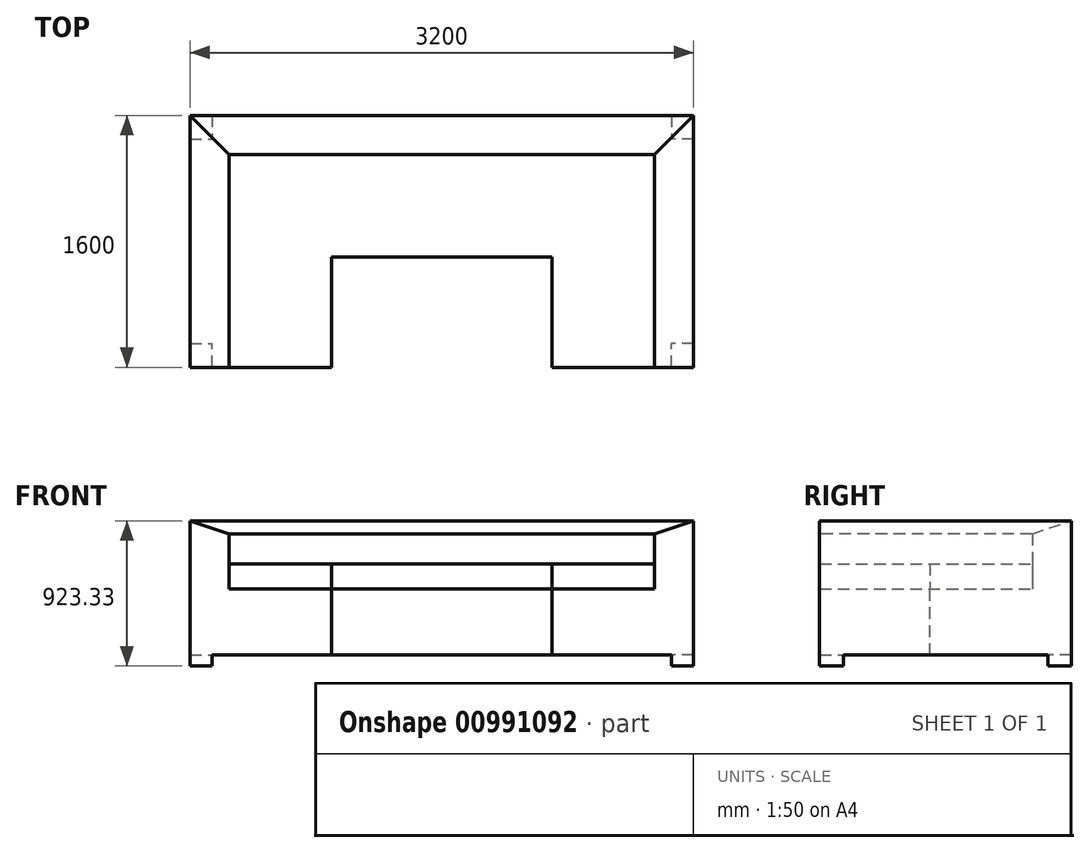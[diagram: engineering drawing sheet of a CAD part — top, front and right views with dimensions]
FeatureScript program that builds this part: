
annotation { "Feature Type Name" : "Feature", "Feature Type Description" : "" }
export const myFeature = defineFeature(function(context is Context, id is Id, definition is map)
    precondition{}
    {
        {
            var Q0;
            Q0=qCreatedBy(makeId("Top.planeOp"),FACE);
            var sketch = newSketch(context, id + "F0", { "sketchPlane" : qUnion([Q0])});
            skLineSegment(sketch, "E0.bottom", {"start": v(0, 0) * mm, "end": v(-900, 0) * mm});
            skLineSegment(sketch, "E0.top", {"start": v(0, 1600) * mm, "end": v(-900, 1600) * mm});
            skLineSegment(sketch, "E0.left", {"start": v(0, 0) * mm, "end": v(0, 1600) * mm});
            skLineSegment(sketch, "E0.right", {"start": v(-900, 0) * mm, "end": v(-900, 700) * mm});
            skLineSegment(sketch, "E1.bottom", {"start": v(-900, 1600) * mm, "end": v(-2300, 1600) * mm});
            skLineSegment(sketch, "E1.top", {"start": v(-900, 700) * mm, "end": v(-2300, 700) * mm});
            skLineSegment(sketch, "E2", {"start": v(-1600, 1600) * mm, "end": v(-1600, 700) * mm, "construction": true});
            skLineSegment(sketch, "E3.MirrorCS", {"start": v(-3200, 1600) * mm, "end": v(-2300, 1600) * mm});
            skLineSegment(sketch, "E4.MirrorCS", {"start": v(-3200, 0) * mm, "end": v(-3200, 1600) * mm});
            skLineSegment(sketch, "E5.MirrorCS", {"start": v(-3200, 0) * mm, "end": v(-2300, 0) * mm});
            skLineSegment(sketch, "E6.MirrorCS", {"start": v(-2300, 0) * mm, "end": v(-2300, 700) * mm});
            skPoint(sketch, "E7.MirrorCS.end.orphan", {"position": v(-2300, 700) * mm});
            skPoint(sketch, "E7.MirrorCS.start.orphan", {"position": v(-2300, 1600) * mm});
            skLineSegment(sketch, "E8.0", {"start": v(-250, 0) * mm, "end": v(-250, 1350) * mm});
            skLineSegment(sketch, "E8.1", {"start": v(-2950, 0) * mm, "end": v(-2950, 1350) * mm});
            skLineSegment(sketch, "E8.2", {"start": v(-2950, 1350) * mm, "end": v(-1600, 1350) * mm});
            skLineSegment(sketch, "E8.3", {"start": v(-900, 1350) * mm, "end": v(-1600, 1350) * mm});
            skLineSegment(sketch, "E8.4", {"start": v(-250, 1350) * mm, "end": v(-900, 1350) * mm});
            skLineSegment(sketch, "E9", {"start": v(-900, 1600) * mm, "end": v(-900, 700) * mm, "construction": true});
            skLineSegment(sketch, "E10", {"start": v(-3200, 1480.04) * mm, "end": v(0, 1480.04) * mm, "construction": true});
            skSolve(sketch);
        }
        {
            var Q0;
            Q0 = qSketchRegion(id + "F0", true);
            extrude(context, id + "F1", {"entities" : qUnion([Q0]), "oppositeDirection" : true, "depth" : 420 * mm, "offsetDistance" : 25 * mm});
        }
        {
            var Q0;
            Q0=makeQuery(id+"F0.imprint","IMPRINT",FACE,{"disambiguationData":[TD([[makeQuery(id+"F0.imprint","IMPRINT",EDGE,{"derivedFrom":sQuery(id+"F0.wireOp",EDGE,"E0.top")}),1.0]])]});
            extrude(context, id + "F2", {"entities" : qUnion([Q0]), "operationType" : NewBodyOperationType.ADD, "depth" : 450 * mm, "offsetDistance" : 25 * mm});
        }
        {
            var Q0;
            Q0=makeQuery(id+"F2.opExtrude","CAP_EDGE",EDGE,{"disambiguationData":[OSD([sQuery(id+"F0.wireOp",EDGE,"E8.0")])],"isStart":false});
            var Q1;
            Q1=makeQuery(id+"F2.opExtrude","CAP_EDGE",EDGE,{"disambiguationData":[OSD([sQuery(id+"F0.wireOp",EDGE,"E8.3"),sQuery(id+"F0.wireOp",EDGE,"E8.4")])],"isStart":false});
            var Q2;
            Q2=makeQuery(id+"F2.opExtrude","CAP_EDGE",EDGE,{"disambiguationData":[OSD([sQuery(id+"F0.wireOp",EDGE,"E8.2")])],"isStart":false});
            var Q3;
            Q3=makeQuery(id+"F2.opExtrude","CAP_EDGE",EDGE,{"disambiguationData":[OSD([sQuery(id+"F0.wireOp",EDGE,"E8.1")])],"isStart":false});
            chamfer(context, id + "F3", {"entities" : qUnion([Q0, Q1, Q2, Q3]), "chamferType" : ChamferType.TWO_OFFSETS, "width1" : 300 * mm, "oppositeDirection" : false, "width2" : 100 * mm, "tangentPropagation" : true});
        }
        {
            var Q0;
            {var subQ3=sQuery(id+"F0.wireOp",EDGE,"E0.right");Q0=makeQuery(id+"F0.imprint","IMPRINT",FACE,{"disambiguationData":[TD([[makeQuery(id+"F0.imprint","IMPRINT",EDGE,{"derivedFrom":subQ3}),-1.0]])]});}
            extrude(context, id + "F4", {"entities" : qUnion([Q0]), "depth" : 160 * mm, "offsetDistance" : 25 * mm});
        }
        {
            var Q0;
            Q0=makeQuery(id+"F1.opExtrude","CAP_FACE",FACE,{"disambiguationData":[OSD([sQuery(id+"F0.wireOp",EDGE,"E0.bottom"),sQuery(id+"F0.wireOp",EDGE,"E0.top"),sQuery(id+"F0.wireOp",EDGE,"E0.left"),sQuery(id+"F0.wireOp",EDGE,"E0.right"),sQuery(id+"F0.wireOp",EDGE,"E1.bottom"),sQuery(id+"F0.wireOp",EDGE,"E1.top"),sQuery(id+"F0.wireOp",EDGE,"E3.MirrorCS"),sQuery(id+"F0.wireOp",EDGE,"E4.MirrorCS"),sQuery(id+"F0.wireOp",EDGE,"E5.MirrorCS"),sQuery(id+"F0.wireOp",EDGE,"E6.MirrorCS")])],"isStart":false});
            var sketch = newSketch(context, id + "F5", { "sketchPlane" : qUnion([Q0])});
            skLineSegment(sketch, "E11.bottom", {"start": v(-3200, -1600) * mm, "end": v(-3059.88, -1600) * mm});
            skLineSegment(sketch, "E11.top", {"start": v(-3200, -1450) * mm, "end": v(-3059.88, -1450) * mm});
            skLineSegment(sketch, "E11.left", {"start": v(-3200, -1600) * mm, "end": v(-3200, -1450) * mm});
            skLineSegment(sketch, "E11.right", {"start": v(-3059.88, -1600) * mm, "end": v(-3059.88, -1450) * mm});
            skLineSegment(sketch, "E12.MirrorCS", {"start": v(0, -1450) * mm, "end": v(-140.12, -1450) * mm});
            skLineSegment(sketch, "E13.MirrorCS", {"start": v(-140.12, -1600) * mm, "end": v(-140.12, -1450) * mm});
            skLineSegment(sketch, "E14.MirrorCS", {"start": v(0, -1600) * mm, "end": v(0, -1450) * mm});
            skLineSegment(sketch, "E15.MirrorCS", {"start": v(0, -1600) * mm, "end": v(-140.12, -1600) * mm});
            skLineSegment(sketch, "E16", {"start": v(-3200, -800) * mm, "end": v(-2019.08, -800) * mm, "construction": true});
            skLineSegment(sketch, "E17.MirrorCS", {"start": v(0, 0) * mm, "end": v(0, -150) * mm});
            skLineSegment(sketch, "E18.MirrorCS", {"start": v(0, -150) * mm, "end": v(-140.12, -150) * mm});
            skLineSegment(sketch, "E19.MirrorCS", {"start": v(-140.12, 0) * mm, "end": v(-140.12, -150) * mm});
            skLineSegment(sketch, "E20.MirrorCS", {"start": v(0, 0) * mm, "end": v(-140.12, 0) * mm});
            skLineSegment(sketch, "E21.MirrorCS", {"start": v(-3200, 0) * mm, "end": v(-3200, -150) * mm});
            skLineSegment(sketch, "E22.MirrorCS", {"start": v(-3200, -150) * mm, "end": v(-3059.88, -150) * mm});
            skLineSegment(sketch, "E23.MirrorCS", {"start": v(-3059.88, 0) * mm, "end": v(-3059.88, -150) * mm});
            skLineSegment(sketch, "E24.MirrorCS", {"start": v(-3200, 0) * mm, "end": v(-3059.88, 0) * mm});
            skSolve(sketch);
        }
        {
            var Q0;
            Q0 = qSketchRegion(id + "F5", true);
            extrude(context, id + "F6", {"entities" : qUnion([Q0]), "operationType" : NewBodyOperationType.ADD, "depth" : 70 * mm, "offsetDistance" : 25 * mm});
        }
    });
